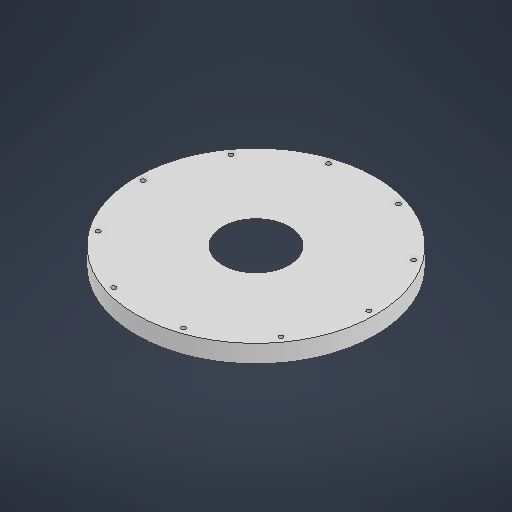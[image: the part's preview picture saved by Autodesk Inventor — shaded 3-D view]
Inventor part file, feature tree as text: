
AUTODESK INVENTOR PART (.ipt)
format: ipt  version: 2025 (Build 290162000, 162)  size: 213,504 bytes
history: native  units: in
note: dims shown in document units (in); Inventor stores cm internally (conversion verified against a paired STEP export)
features: sketch x4, extrude x2, hole x1
ambient origin geometry x8: Origin, YZ Plane, XZ Plane, XY Plane, X Axis, Y Axis, Z Axis, Center Point
bodies: Solid1 (feature_tree)
feature tree (7):
  extrude  "Extrusion1"  Depth=8.6614in
  extrude  "Extrusion2"  Depth=0.7874in
  hole  "Hole1"  [1 undecoded]
  sketch  "Sketch1"  dims[d0=10.6299in d1=8.6614in]
  sketch  "Sketch2"  dims[d5=0.0394in d6=0.0in d7=10.0394in]
  sketch  "Sketch3"  dims[d8=0.1969in d9=3.937in d11=360.0deg d13=0.1969in d14=0.2362in d15=0.1575in d16=0.0787in d17=90.0deg d18=0.315in d19=0.8108in d20=10.6299in]
  sketch  "Sketch Circular Pattern1"  dims[d2=0.7874in d3=0.0in d4=2.9528in]
note: 1 required parameter value undecoded (feature->parameter linkage not recoverable at this tier; creation-order binding heuristic only, values carry confidence <= 0.55)
